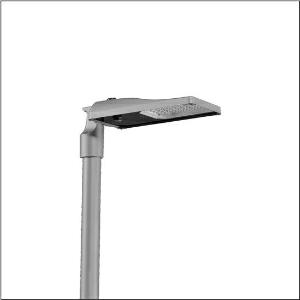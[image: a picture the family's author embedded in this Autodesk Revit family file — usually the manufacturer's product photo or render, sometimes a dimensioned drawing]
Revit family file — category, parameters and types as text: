
# Revit family: streetlight_sl_31_mini___st0_8a_5xh6c31t08ha_0974
name_source: partatom
category: Lighting Fixtures
units: mm (PartAtom-declared; Revit-internal decimal feet)

## family parameters
Cut with Voids When Loaded = No
Host = Face
Light Source = No
Part Type = Normal
Room Calculation Point = No
Round Connector Dimension = Use Diameter
Shared = No

## types (1)
- --- (1 x LED, 9230 lm, 68.2 W, 3000K)
    Apparent Load = 68 VA
    CIE Flux Codes = 38 75 97 100 100
    Color Rendering = 70
    Color Temperature = 3000K
    Default Elevation = 1800 mm
    Description = Streetlight SL 31 mini, mast luminaire, primary light control with lens, of PMMA, primary optical cover: cover, of toughened safety glass, transparent, light distribution: ST0.8a, light emission: direct distribution, primary light characteristic: asymmetric, installation type: post-top, side-entry, LED, High Power LED, rated luminous flux: 9.230lm, luminous efficacy: 135lm/W, light colour: 730, colour temperature: 3000K, control: presetting dimming logarithmic, flexible luminous flux parameterisation, time-dependent luminous flux control, constant luminous flux control, power reduction, intelligent temperature release in ECG and LED module, overheat protection, with cable H07RN-F 2x 1.5mm², mains connection: 220..240V, AC, 50/60Hz, connection cable pre-assembled, cable length: 8,5m, start of lifetime: 68W, end of service life: 74W, reduction: 30W, luminaire housing, of diecast aluminium, powder-coated, Siteco® metallic grey (DB 702S), corrosivity category C5 high according to DIN EN ISO 12944, sealing non-destructively replaceable, multi-level sealing system, mast flange (76/60mm) included as standard, inclination: -15°..+20° (post-top) | -20°..+20° (side-entry), adjustable in 5° steps, no sealing on luminaire upper side, Smart Interface below and above, protection rating (complete): IP66, insulation class (complete): insulation class II (safety insulation), certification: CE, ENEC, ENEC+, VDE, UKCA, ZD4i, impact resistance: IK09, permissible operating ambient temperature for outdoor applications: -40..+50°C, standard-compliant lighting for roads and squares, packaging unit: 1 piece

Light Distribution: ST0.8a
    Height = 76 mm
    Lamp = 1 x LED
    Lamp Light Flux = 9230 lm
    Lamp Power = 68.2 W
    Lamp count = 1
    Length = 547 mm
    Luminous efficacy = 135 lm/W
    Manufacturer = Siteco
    ModVariant = No
    Model = 5XH6C31T08HA
    Number of Poles = 1
    OnlyDefault = Yes
    Power Factor = 1
    Product Name = Streetlight SL 31 mini | ST0.8a
    Product group = mast luminaire | pylon top
    ProductGroupID = 6100
    Protection Class = Protection class II
    Protection Degree = IP 66
    RLX_Detail_Level = 1
    RLX_Emergency_Light_Flux = 0 lm
    RLX_Emergency_Type = 0
    RLX_Emergency_Type_DB = No
    RlxData = <blob elided: 39841 chars, md5=579ae23e>
    Socket = socket
    Standby Power = 0 W
    System Light Flux = 9230 lm
    System Power = 68 W
    Type Comments = factory setting: luminous flux: 100 % | dim-lin: 254 | 692 mA
    Type Image = l_1300332.jpg
    URL = http://relux.com
    VarID = @adj_007231
    Voltage = 0 V
    Weight = 0.00 kg
    Width = 265 mm

## geometry (parser evidence)
native form markers: Blend x4, Sweep x9
no freeform markers — native parametric forms only
